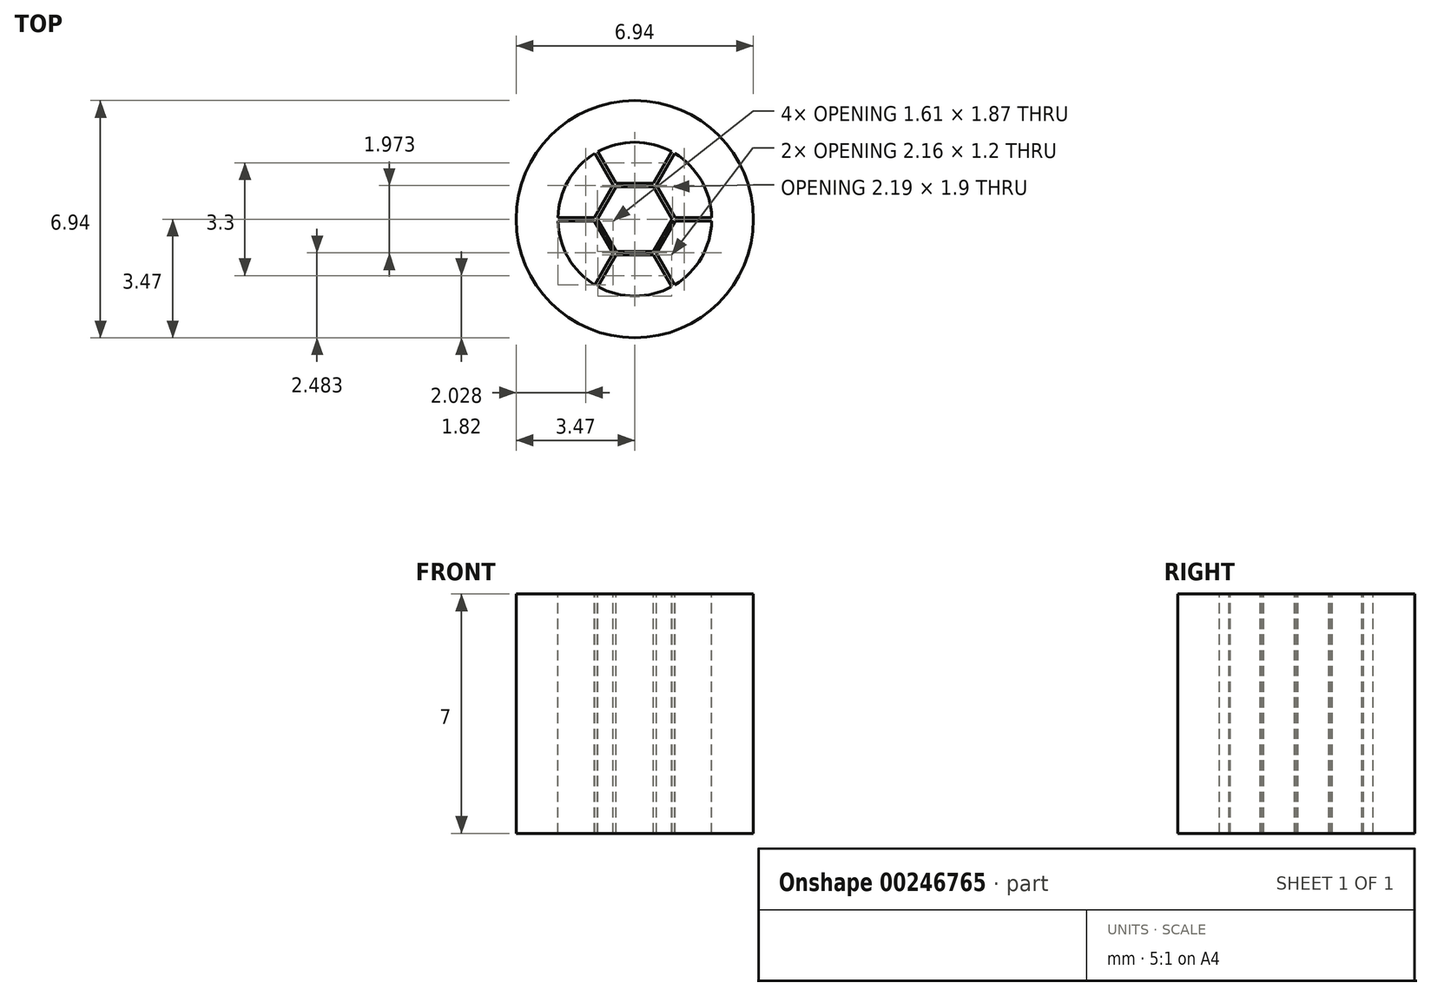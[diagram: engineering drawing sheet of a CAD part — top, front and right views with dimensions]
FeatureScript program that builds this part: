
annotation { "Feature Type Name" : "Feature", "Feature Type Description" : "" }
export const myFeature = defineFeature(function(context is Context, id is Id, definition is map)
    precondition{}
    {
        {
            var Q0;
            Q0=qCreatedBy(makeId("Top.planeOp"),FACE);
            var sketch = newSketch(context, id + "F0", { "sketchPlane" : qUnion([Q0])});
            skCircle(sketch, "E0", {"center": v(0, 0) * mm, "radius": 3.47 * mm});
            skSolve(sketch);
        }
        {
            var Q0;
            Q0=makeQuery(id+"F0.imprint","IMPRINT",FACE,{"disambiguationData":[TD([[makeQuery(id+"F0.imprint","IMPRINT",EDGE,{"derivedFrom":sQuery(id+"F0.wireOp",EDGE,"E0")}),1.0]])]});
            extrude(context, id + "F1", {"entities" : qUnion([Q0]), "depth" : 7 * mm});
        }
        {
            var Q0;
            Q0=makeQuery(id+"F1.opExtrude","CAP_FACE",FACE,{"disambiguationData":[OSD([sQuery(id+"F0.wireOp",EDGE,"E0")])],"isStart":false});
            var sketch = newSketch(context, id + "F2", { "sketchPlane" : qUnion([Q0])});
            skCircle(sketch, "E1.cCircle", {"center": v(0, 0) * mm, "radius": 0.95 * mm, "construction": true});
            skLineSegment(sketch, "E1.0", {"start": v(0.55, -0.95) * mm, "end": v(-0.55, -0.95) * mm});
            skLineSegment(sketch, "E1.1", {"start": v(-0.55, -0.95) * mm, "end": v(-1.1, 0) * mm});
            skLineSegment(sketch, "E1.2", {"start": v(-1.1, 0) * mm, "end": v(-0.55, 0.95) * mm});
            skLineSegment(sketch, "E1.3", {"start": v(-0.55, 0.95) * mm, "end": v(0.55, 0.95) * mm});
            skLineSegment(sketch, "E1.4", {"start": v(0.55, 0.95) * mm, "end": v(1.1, 0) * mm});
            skLineSegment(sketch, "E1.5", {"start": v(1.1, 0) * mm, "end": v(0.55, -0.95) * mm});
            skPoint(sketch, "E1.0.midPoint", {"position": v(0, -0.95) * mm});
            skLineSegment(sketch, "E2.1.0.0", {"start": v(-0.55, 1.05) * mm, "end": v(-1.1, 2) * mm});
            skPoint(sketch, "E2.1.0.1", {"position": v(0, 1.05) * mm});
            skLineSegment(sketch, "E2.1.0.2", {"start": v(-0.55, 2.95) * mm, "end": v(0.55, 2.95) * mm});
            skCircle(sketch, "E2.1.0.3", {"center": v(0, 2) * mm, "radius": 0.95 * mm, "construction": true});
            skLineSegment(sketch, "E2.1.0.4", {"start": v(0.55, 1.05) * mm, "end": v(-0.55, 1.05) * mm});
            skLineSegment(sketch, "E2.1.0.5", {"start": v(-1.1, 2) * mm, "end": v(-0.55, 2.95) * mm});
            skLineSegment(sketch, "E2.1.0.6", {"start": v(1.1, 2) * mm, "end": v(0.55, 1.05) * mm});
            skLineSegment(sketch, "E2.1.0.7", {"start": v(0.55, 2.95) * mm, "end": v(1.1, 2) * mm});
            skLineSegment(sketch, "E2.direction1", {"start": v(-0.55, -0.95) * mm, "end": v(-0.55, 1.05) * mm, "construction": true});
            skPoint(sketch, "E3.1.0", {"position": v(-0.9, 0.53) * mm});
            skLineSegment(sketch, "E3.1.1", {"start": v(-0.64, 1) * mm, "end": v(-1.18, 0.05) * mm});
            skLineSegment(sketch, "E3.1.2", {"start": v(-1.18, 1.95) * mm, "end": v(-0.64, 1) * mm});
            skLineSegment(sketch, "E3.1.3", {"start": v(-2.28, 1.95) * mm, "end": v(-1.18, 1.95) * mm});
            skLineSegment(sketch, "E3.1.4", {"start": v(-2.28, 0.05) * mm, "end": v(-2.83, 1) * mm});
            skLineSegment(sketch, "E3.1.5", {"start": v(-2.83, 1) * mm, "end": v(-2.28, 1.95) * mm});
            skCircle(sketch, "E3.1.6", {"center": v(-1.73, 1) * mm, "radius": 0.95 * mm, "construction": true});
            skLineSegment(sketch, "E3.1.7", {"start": v(-1.18, 0.05) * mm, "end": v(-2.28, 0.05) * mm});
            skPoint(sketch, "E3.2.0", {"position": v(-0.9, -0.52) * mm});
            skLineSegment(sketch, "E3.2.1", {"start": v(-1.18, -0.05) * mm, "end": v(-0.64, -1) * mm});
            skLineSegment(sketch, "E3.2.2", {"start": v(-2.28, -0.05) * mm, "end": v(-1.18, -0.05) * mm});
            skLineSegment(sketch, "E3.2.3", {"start": v(-2.83, -1) * mm, "end": v(-2.28, -0.05) * mm});
            skLineSegment(sketch, "E3.2.4", {"start": v(-1.18, -1.95) * mm, "end": v(-2.28, -1.95) * mm});
            skLineSegment(sketch, "E3.2.5", {"start": v(-2.28, -1.95) * mm, "end": v(-2.83, -1) * mm});
            skCircle(sketch, "E3.2.6", {"center": v(-1.73, -1) * mm, "radius": 0.95 * mm, "construction": true});
            skLineSegment(sketch, "E3.2.7", {"start": v(-0.64, -1) * mm, "end": v(-1.18, -1.95) * mm});
            skPoint(sketch, "E3.3.0", {"position": v(0, -1.05) * mm});
            skLineSegment(sketch, "E3.3.1", {"start": v(-0.55, -1.05) * mm, "end": v(0.55, -1.05) * mm});
            skLineSegment(sketch, "E3.3.2", {"start": v(-1.1, -2) * mm, "end": v(-0.55, -1.05) * mm});
            skLineSegment(sketch, "E3.3.3", {"start": v(-0.55, -2.95) * mm, "end": v(-1.1, -2) * mm});
            skLineSegment(sketch, "E3.3.4", {"start": v(1.1, -2) * mm, "end": v(0.55, -2.95) * mm});
            skLineSegment(sketch, "E3.3.5", {"start": v(0.55, -2.95) * mm, "end": v(-0.55, -2.95) * mm});
            skCircle(sketch, "E3.3.6", {"center": v(0, -2) * mm, "radius": 0.95 * mm, "construction": true});
            skLineSegment(sketch, "E3.3.7", {"start": v(0.55, -1.05) * mm, "end": v(1.1, -2) * mm});
            skPoint(sketch, "E3.4.0", {"position": v(0.9, -0.53) * mm});
            skLineSegment(sketch, "E3.4.1", {"start": v(0.64, -1) * mm, "end": v(1.18, -0.05) * mm});
            skLineSegment(sketch, "E3.4.2", {"start": v(1.18, -1.95) * mm, "end": v(0.64, -1) * mm});
            skLineSegment(sketch, "E3.4.3", {"start": v(2.28, -1.95) * mm, "end": v(1.18, -1.95) * mm});
            skLineSegment(sketch, "E3.4.4", {"start": v(2.28, -0.05) * mm, "end": v(2.83, -1) * mm});
            skLineSegment(sketch, "E3.4.5", {"start": v(2.83, -1) * mm, "end": v(2.28, -1.95) * mm});
            skCircle(sketch, "E3.4.6", {"center": v(1.73, -1) * mm, "radius": 0.95 * mm, "construction": true});
            skLineSegment(sketch, "E3.4.7", {"start": v(1.18, -0.05) * mm, "end": v(2.28, -0.05) * mm});
            skPoint(sketch, "E3.5.0", {"position": v(0.9, 0.53) * mm});
            skLineSegment(sketch, "E3.5.1", {"start": v(1.18, 0.05) * mm, "end": v(0.64, 1) * mm});
            skLineSegment(sketch, "E3.5.2", {"start": v(2.28, 0.05) * mm, "end": v(1.18, 0.05) * mm});
            skLineSegment(sketch, "E3.5.3", {"start": v(2.83, 1) * mm, "end": v(2.28, 0.05) * mm});
            skLineSegment(sketch, "E3.5.4", {"start": v(1.18, 1.95) * mm, "end": v(2.28, 1.95) * mm});
            skLineSegment(sketch, "E3.5.5", {"start": v(2.28, 1.95) * mm, "end": v(2.83, 1) * mm});
            skCircle(sketch, "E3.5.6", {"center": v(1.73, 1) * mm, "radius": 0.95 * mm, "construction": true});
            skLineSegment(sketch, "E3.5.7", {"start": v(0.64, 1) * mm, "end": v(1.18, 1.95) * mm});
            skCircle(sketch, "E4", {"center": v(0, 0) * mm, "radius": 2.25 * mm});
            skSolve(sketch);
        }
        {
            var Q0;
            Q0=makeQuery(id+"F2.imprint","IMPRINT",FACE,{"disambiguationData":[TD([[makeQuery(id+"F2.imprint","IMPRINT",EDGE,{"derivedFrom":sQuery(id+"F2.wireOp",EDGE,"E3.1.1")}),-1.0]])]});
            var Q1;
            Q1=makeQuery(id+"F2.imprint","IMPRINT",FACE,{"disambiguationData":[TD([[makeQuery(id+"F2.imprint","IMPRINT",EDGE,{"derivedFrom":sQuery(id+"F2.wireOp",EDGE,"E2.1.0.0")}),-1.0]])]});
            var Q2;
            Q2=makeQuery(id+"F2.imprint","IMPRINT",FACE,{"disambiguationData":[TD([[makeQuery(id+"F2.imprint","IMPRINT",EDGE,{"derivedFrom":sQuery(id+"F2.wireOp",EDGE,"E3.5.1")}),-1.0]])]});
            var Q3;
            Q3=makeQuery(id+"F2.imprint","IMPRINT",FACE,{"disambiguationData":[TD([[makeQuery(id+"F2.imprint","IMPRINT",EDGE,{"derivedFrom":sQuery(id+"F2.wireOp",EDGE,"E1.0")}),-1.0]])]});
            var Q4;
            Q4=makeQuery(id+"F2.imprint","IMPRINT",FACE,{"disambiguationData":[TD([[makeQuery(id+"F2.imprint","IMPRINT",EDGE,{"derivedFrom":sQuery(id+"F2.wireOp",EDGE,"E3.4.1")}),-1.0]])]});
            var Q5;
            Q5=makeQuery(id+"F2.imprint","IMPRINT",FACE,{"disambiguationData":[TD([[makeQuery(id+"F2.imprint","IMPRINT",EDGE,{"derivedFrom":sQuery(id+"F2.wireOp",EDGE,"E3.3.1")}),-1.0]])]});
            var Q6;
            Q6=makeQuery(id+"F2.imprint","IMPRINT",FACE,{"disambiguationData":[TD([[makeQuery(id+"F2.imprint","IMPRINT",EDGE,{"derivedFrom":sQuery(id+"F2.wireOp",EDGE,"E3.2.1")}),-1.0]])]});
            extrude(context, id + "F3", {"entities" : qUnion([Q0, Q1, Q2, Q3, Q4, Q5, Q6]), "operationType" : NewBodyOperationType.REMOVE, "oppositeDirection" : true, "depth" : 7 * mm});
        }
    });
